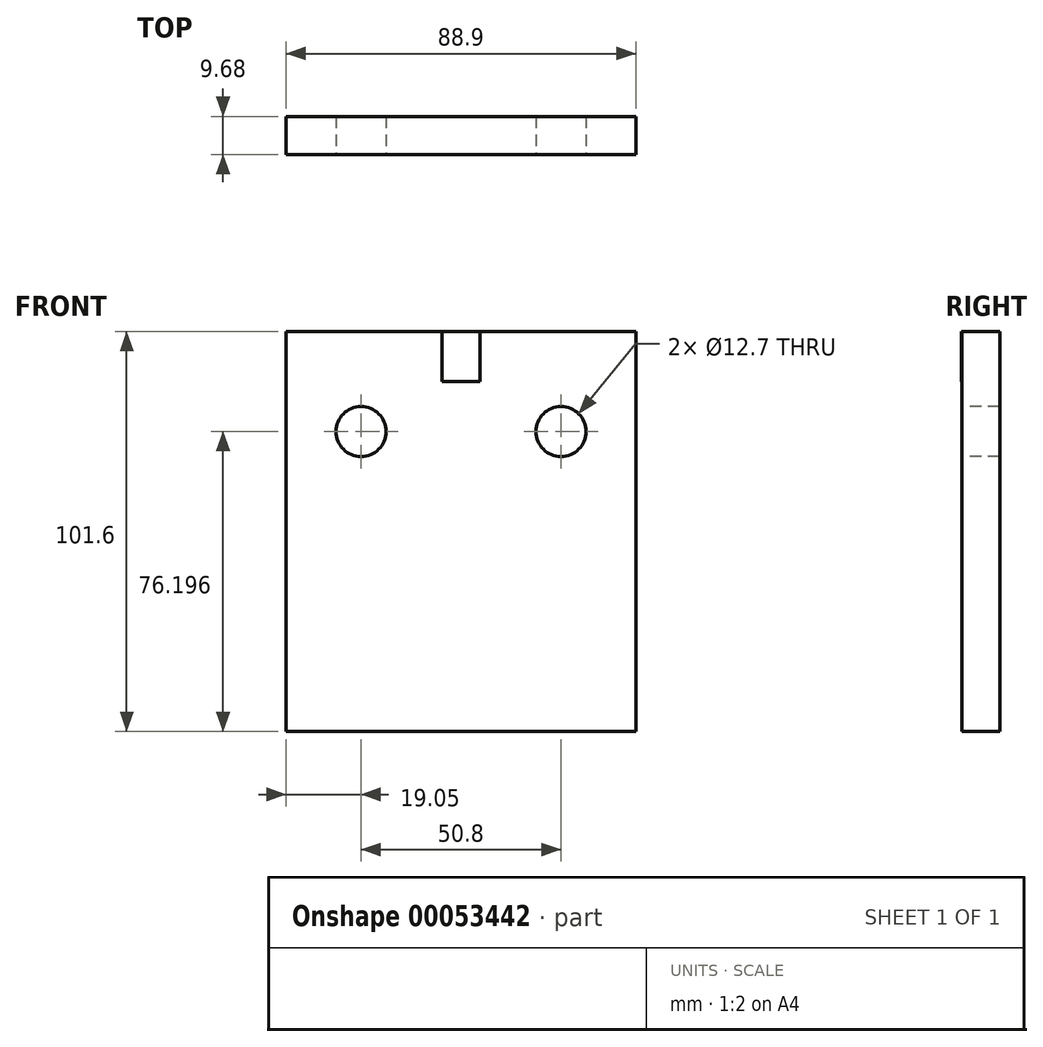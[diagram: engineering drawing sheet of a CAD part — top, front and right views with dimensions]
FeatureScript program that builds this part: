
annotation { "Feature Type Name" : "Feature", "Feature Type Description" : "" }
export const myFeature = defineFeature(function(context is Context, id is Id, definition is map)
    precondition{}
    {
        {
            var Q0;
            Q0=qCreatedBy(makeId("Front.planeOp"),FACE);
            var sketch = newSketch(context, id + "F0", { "sketchPlane" : qUnion([Q0])});
            skLineSegment(sketch, "E0.bottom", {"start": v(19.05, -45.8) * mm, "end": v(-69.85, -45.8) * mm});
            skLineSegment(sketch, "E0.top", {"start": v(19.05, 55.8) * mm, "end": v(-69.85, 55.8) * mm});
            skLineSegment(sketch, "E0.left", {"start": v(19.05, -45.8) * mm, "end": v(19.05, 55.8) * mm});
            skLineSegment(sketch, "E0.right", {"start": v(-69.85, -45.8) * mm, "end": v(-69.85, 55.8) * mm});
            skCircle(sketch, "E1", {"center": v(0, 30.4) * mm, "radius": 6.35 * mm});
            skCircle(sketch, "E2", {"center": v(-50.8, 30.4) * mm, "radius": 6.35 * mm});
            skLineSegment(sketch, "E3", {"start": v(-25.4, 55.8) * mm, "end": v(-30.23, 55.8) * mm});
            skLineSegment(sketch, "E4", {"start": v(-25.4, 55.8) * mm, "end": v(-20.57, 55.8) * mm});
            skPoint(sketch, "E5", {"position": v(-20.57, 55.8) * mm});
            skPoint(sketch, "E6", {"position": v(-30.23, 55.8) * mm});
            skLineSegment(sketch, "E7.bottom", {"start": v(-30.23, 55.8) * mm, "end": v(-20.57, 55.8) * mm});
            skLineSegment(sketch, "E7.top", {"start": v(-30.23, 41.8) * mm, "end": v(-20.57, 41.8) * mm});
            skLineSegment(sketch, "E7.left", {"start": v(-30.23, 55.8) * mm, "end": v(-30.23, 41.8) * mm});
            skLineSegment(sketch, "E7.right", {"start": v(-20.57, 55.8) * mm, "end": v(-20.57, 41.8) * mm});
            skSolve(sketch);
        }
        {
            var Q0;
            Q0=makeQuery(id+"F0.imprint","IMPRINT",FACE,{"disambiguationData":[TD([[makeQuery(id+"F0.imprint","IMPRINT",EDGE,{"derivedFrom":sQuery(id+"F0.wireOp",EDGE,"E0.bottom")}),-1.0]])]});
            var Q1;
            Q1=makeQuery(id+"F0.imprint","IMPRINT",FACE,{"disambiguationData":[TD([[makeQuery(id+"F0.imprint","IMPRINT",EDGE,{"derivedFrom":sQuery(id+"F0.wireOp",EDGE,"E7.top")}),1.0]])]});
            extrude(context, id + "F1", {"entities" : qUnion([Q0, Q1]), "oppositeDirection" : true, "depth" : 9.65 * mm});
        }
        {
            var Q0;
            Q0=makeQuery(id+"F1.opExtrude","CAP_FACE",FACE,{"disambiguationData":[OSD([sQuery(id+"F0.wireOp",EDGE,"E0.bottom"),sQuery(id+"F0.wireOp",EDGE,"E0.top"),sQuery(id+"F0.wireOp",EDGE,"E0.left"),sQuery(id+"F0.wireOp",EDGE,"E0.right"),sQuery(id+"F0.wireOp",EDGE,"E1"),sQuery(id+"F0.wireOp",EDGE,"E2"),sQuery(id+"F0.wireOp",EDGE,"E7.bottom")])],"isStart":false});
            var sketch = newSketch(context, id + "F2", { "sketchPlane" : qUnion([Q0])});
            skLineSegment(sketch, "E8.bottom", {"start": v(30.23, 55.8) * mm, "end": v(20.57, 55.8) * mm});
            skLineSegment(sketch, "E8.top", {"start": v(30.23, 43.1) * mm, "end": v(20.57, 43.1) * mm});
            skLineSegment(sketch, "E8.left", {"start": v(30.23, 55.8) * mm, "end": v(30.23, 43.1) * mm});
            skLineSegment(sketch, "E8.right", {"start": v(20.57, 55.8) * mm, "end": v(20.57, 43.1) * mm});
            skSolve(sketch);
        }
        {
            var Q0;
            Q0=makeQuery(id+"F2.imprint","IMPRINT",FACE,{"disambiguationData":[TD([[makeQuery(id+"F2.imprint","IMPRINT",EDGE,{"derivedFrom":sQuery(id+"F2.wireOp",EDGE,"E8.bottom")}),-1.0]])]});
            extrude(context, id + "F3", {"entities" : qUnion([Q0]), "operationType" : NewBodyOperationType.ADD, "oppositeDirection" : true, "depth" : 9.68 * mm});
        }
    });
